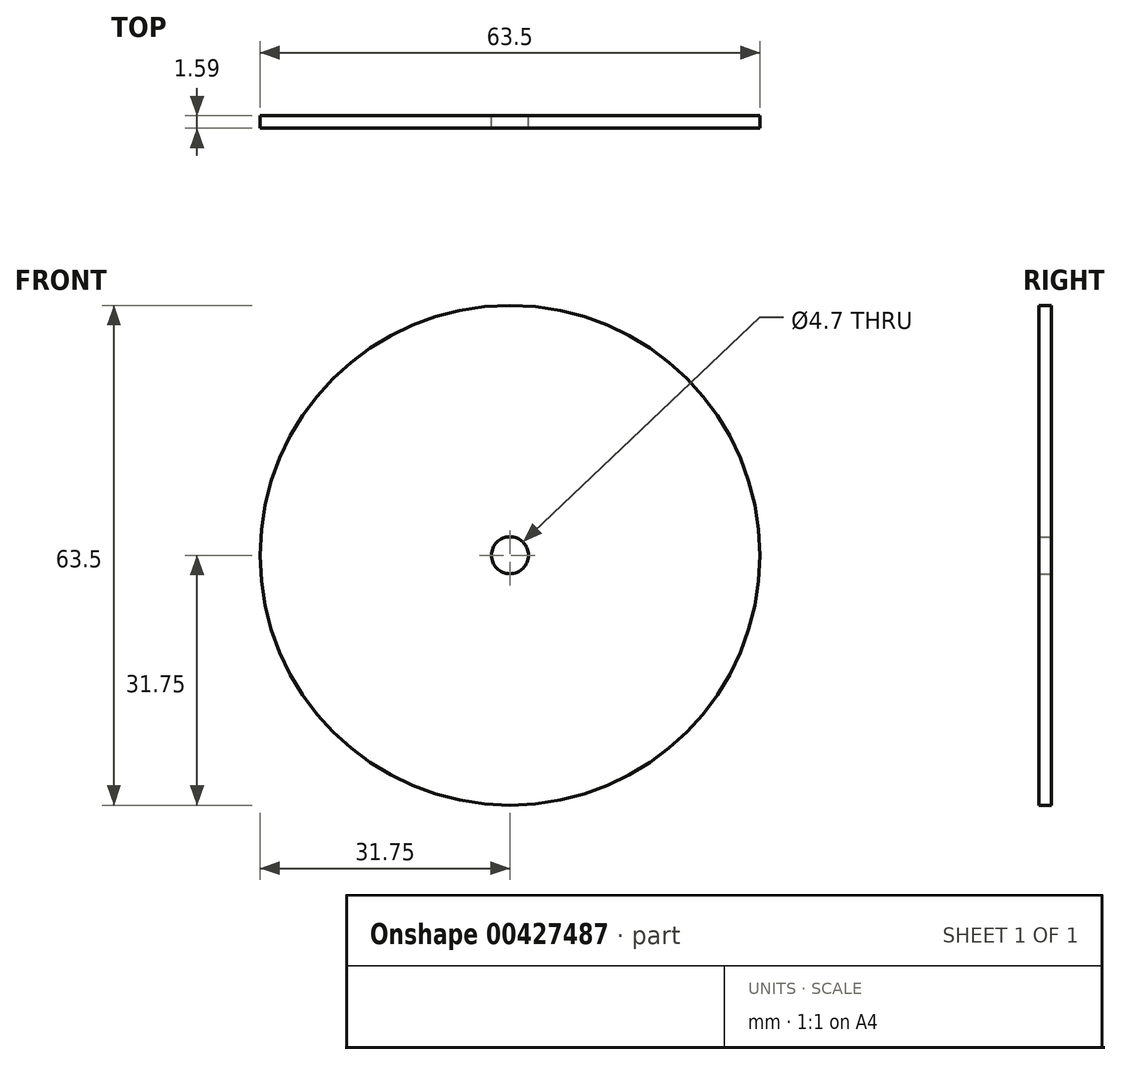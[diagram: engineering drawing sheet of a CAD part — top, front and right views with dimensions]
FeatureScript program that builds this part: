
annotation { "Feature Type Name" : "Feature", "Feature Type Description" : "" }
export const myFeature = defineFeature(function(context is Context, id is Id, definition is map)
    precondition{}
    {
        {
            var Q0;
            Q0=qCreatedBy(makeId("Front.planeOp"),FACE);
            var sketch = newSketch(context, id + "F0", { "sketchPlane" : qUnion([Q0])});
            skCircle(sketch, "E0", {"center": v(0, 0) * mm, "radius": 31.75 * mm});
            skCircle(sketch, "E1", {"center": v(0, 0) * mm, "radius": 2.35 * mm});
            skPoint(sketch, "E2.orphan", {"position": v(0, 2.35) * mm});
            skPoint(sketch, "E3.start.orphan", {"position": v(0, 31.75) * mm});
            skSolve(sketch);
        }
        {
            var Q0;
            Q0=makeQuery(id+"F0.imprint","IMPRINT",FACE,{"disambiguationData":[TD([[makeQuery(id+"F0.imprint","IMPRINT",EDGE,{"derivedFrom":sQuery(id+"F0.wireOp",EDGE,"E0")}),1.0]])]});
            extrude(context, id + "F1", {"entities" : qUnion([Q0]), "depth" : 1.59 * mm});
        }
    });
